# Revit family: Comfort_Window_G_Top_Hung_Standard
name_source: partatom
category: Windows
revit_build: Autodesk Revit 2014 (Build: 20130308_1515(x64)
units: mm (PartAtom-declared; Revit-internal decimal feet)

## types (4) — shared parameters
DG Gasket Thickness = 12 mm  [stored 0.0393701 ft]
Description = Comfort Window, Top Hung, Type G
Double Glazing Gasket Finish = Double Glazing Gasket Material
Frame Depth = 33 mm  [stored 0.108268 ft]
Frame Edge Thickness = 26 mm
Limit Fixed Pane Height Max = 1800 mm  [stored 5.90551 ft]
Limit Fixed Pane Height Min = 200 mm  [stored 0.656168 ft]
Limit Fixed Pane Width Max = 1800 mm  [stored 5.90551 ft]
Limit Fixed Pane Width Min = 200 mm  [stored 0.656168 ft]
Limit Sash Height Max = 1200 mm
Limit Sash Height Min = 300 mm  [stored 0.984252 ft]
Limit Sash Width Max = 1200 mm
Limit Sash Width Min = 300 mm  [stored 0.984252 ft]
Limit Window Height Max = 1852 mm
Manufacturer = Crealco
Max System DG One Piece Thickness = 4 mm  [stored 0.0131234 ft]
Max System DG Unit Thickness = 20 mm  [stored 0.0656168 ft]
Model = Comfort Window
Mullion Width = 27 mm  [stored 0.0885827 ft]
Rough Height = 590 mm  [stored 1.9357 ft]
Rough Width = 902 mm  [stored 2.95932 ft]
Sash Frame Gap = 5 mm  [stored 0.0164042 ft]
Sash Frame Side Gap = 12 mm  [stored 0.0393701 ft]
Sash Side Gap = 38 mm
Set Sash Width = 515 mm  [stored 1.68963 ft]
Transom Height = 27 mm  [stored 0.0885827 ft]
URL = http://www.crealco.co.za
Window Height = 1190 mm  [stored 3.9042 ft]
zero-valued in all types: Visual Light Transmittance

## per-type parameters (varying)
| type | Clearvue SHGC Value | Clearvue U Value | Energy Advantage SHGC Value | Energy Advantage U Value | Intruderprufe LowE SHGC Value | Intruderprufe LowE U Value | Intruderprufe SHGC Value | Intruderprufe U Value | SmartGlass Elite SHGC Value | SmartGlass Elite U Value | SmartGlass Plus SHGC Value | SmartGlass Plus U Value | SmartGlass Standard SHGC Value | SmartGlass Standard U Value | SmartGlass Superior SHGC Value | SmartGlass Superior U Value | Window Width |
| Comfort-1812DT | 0.636 | 6.05 | 0.57 | 4.52 | 0.537 | 4.41 | 0.603 | 5.95 | 0.309 | 3.06 | 0.421 | 3.22 | 0.566 | 3.8 | 0.269 | 3.07 | 1790 mm  [stored 5.8727 ft] |
| Comfort-1212DT | 0.594 | 6.09 | 0.533 | 4.68 | 0.504 | 4.56 | 0.564 | 5.99 | 0.291 | 3.34 | 0.395 | 3.48 | 0.53 | 4.01 | 0.254 | 3.34 | 1190 mm  [stored 3.9042 ft] |
| Comfort-1512DT | 0.632 | 6.06 | 0.567 | 4.53 | 0.534 | 4.42 | 0.6 | 5.95 | 0.307 | 3.08 | 0.419 | 3.24 | 0.562 | 3.82 | 0.267 | 3.09 | 1490 mm  [stored 4.88845 ft] |
| Comfort-2412DT | 0.657 | 6.03 | 0.589 | 4.43 | 0.554 | 4.33 | 0.623 | 5.93 | 0.318 | 2.92 | 0.434 | 3.09 | 0.584 | 3.69 | 0.276 | 2.93 | 2390 mm  [stored 7.84121 ft] |

note: [stored X ft] marks values corroborated as IEEE doubles in the binary element streams (Revit-internal decimal feet)

## geometry (parser evidence)
native form markers: Sweep x17
no freeform markers — native parametric forms only
